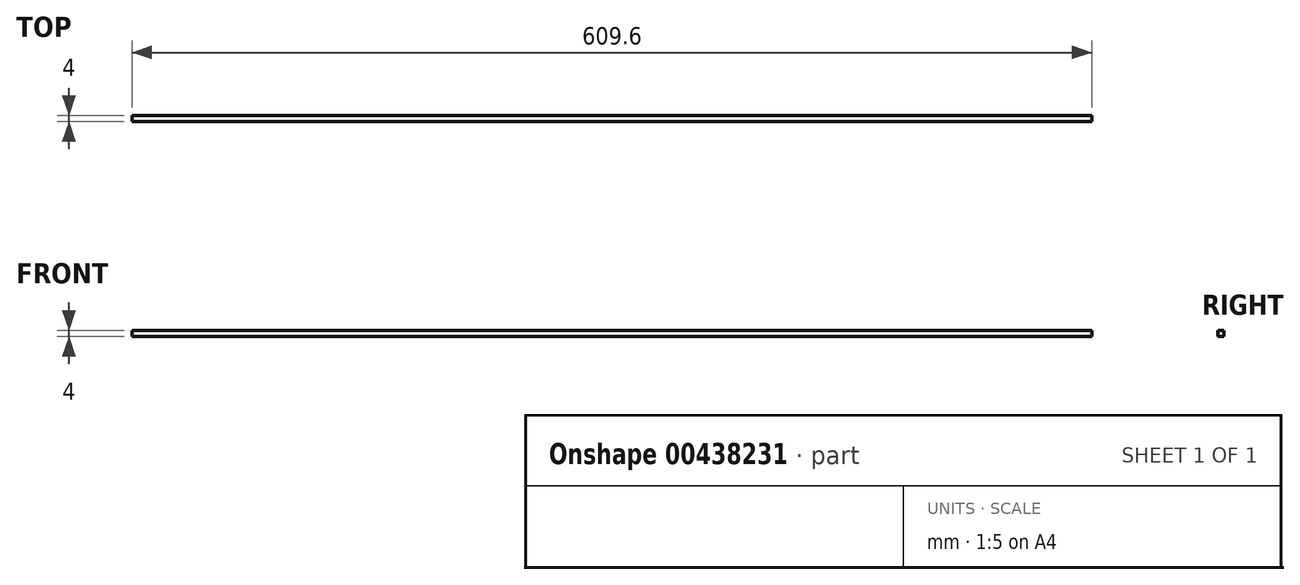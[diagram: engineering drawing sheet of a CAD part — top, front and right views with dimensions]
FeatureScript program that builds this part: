
annotation { "Feature Type Name" : "Feature", "Feature Type Description" : "" }
export const myFeature = defineFeature(function(context is Context, id is Id, definition is map)
    precondition{}
    {
        {
            var Q0;
            Q0=qCreatedBy(makeId("Front.planeOp"),FACE);
            var sketch = newSketch(context, id + "F0", { "sketchPlane" : qUnion([Q0])});
            skLineSegment(sketch, "E0", {"start": v(-297.98, 1.82) * mm, "end": v(311.62, 1.82) * mm});
            skLineSegment(sketch, "E1", {"start": v(311.62, 1.82) * mm, "end": v(311.62, -2.18) * mm});
            skLineSegment(sketch, "E2", {"start": v(311.62, -2.18) * mm, "end": v(-297.98, -2.18) * mm});
            skLineSegment(sketch, "E3", {"start": v(-297.98, -2.18) * mm, "end": v(-297.98, 1.82) * mm});
            skSolve(sketch);
        }
        {
            var Q0;
            Q0 = qSketchRegion(id + "F0", true);
            extrude(context, id + "F1", {"entities" : qUnion([Q0]), "depth" : 4 * mm});
        }
    });
